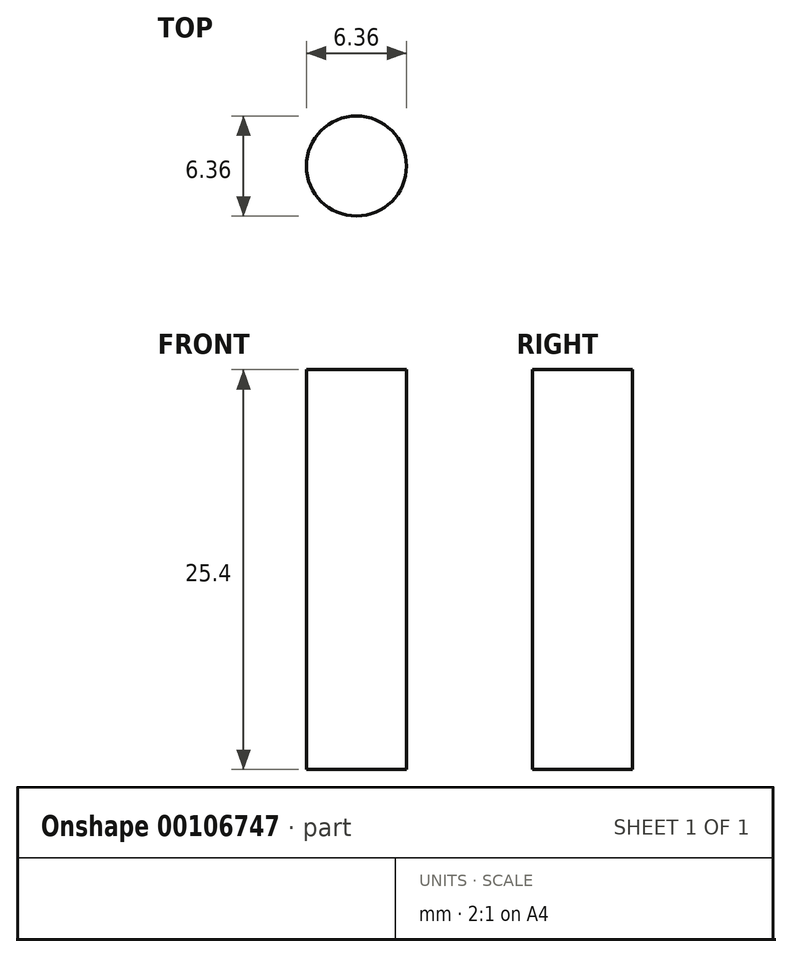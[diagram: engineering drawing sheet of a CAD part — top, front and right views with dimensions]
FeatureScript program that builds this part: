
annotation { "Feature Type Name" : "Feature", "Feature Type Description" : "" }
export const myFeature = defineFeature(function(context is Context, id is Id, definition is map)
    precondition{}
    {
        {
            var Q0;
            Q0=qCreatedBy(makeId("Top.planeOp"),FACE);
            var sketch = newSketch(context, id + "F0", { "sketchPlane" : qUnion([Q0])});
            skCircle(sketch, "E0", {"center": v(0, 0) * mm, "radius": 3.18 * mm});
            skSolve(sketch);
        }
        {
            var Q0;
            Q0 = qSketchRegion(id + "F0", true);
            extrude(context, id + "F1", {"entities" : qUnion([Q0]), "oppositeDirection" : true, "depth" : 25.4 * mm});
        }
    });
